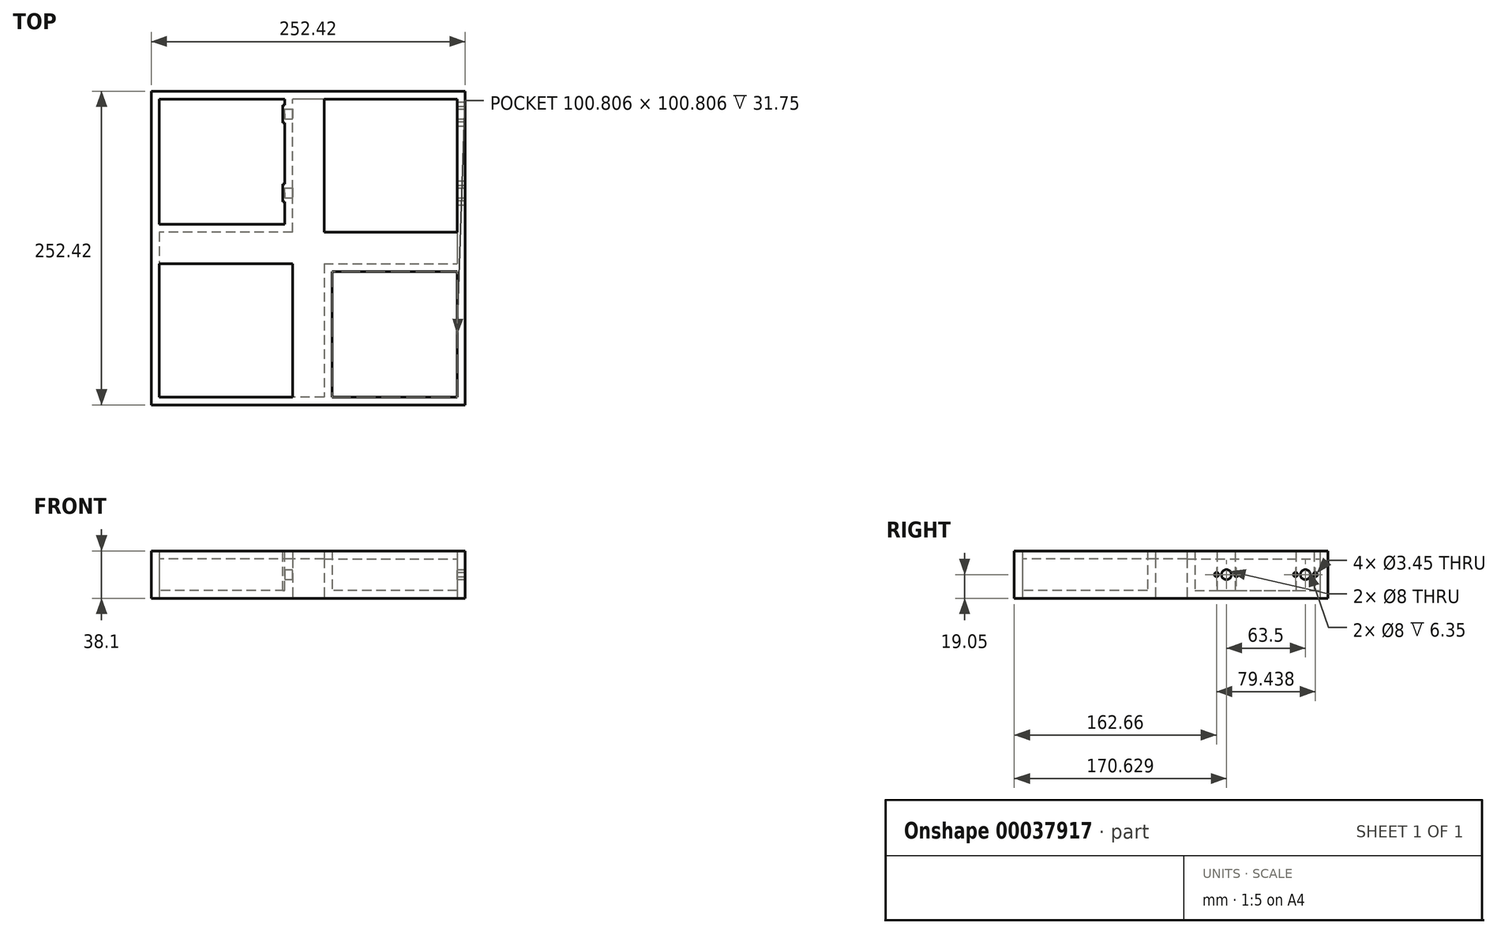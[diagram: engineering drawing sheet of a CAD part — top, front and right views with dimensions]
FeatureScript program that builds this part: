
annotation { "Feature Type Name" : "Feature", "Feature Type Description" : "" }
export const myFeature = defineFeature(function(context is Context, id is Id, definition is map)
    precondition{}
    {
        {
            var Q0;
            Q0=qCreatedBy(makeId("Top.planeOp"),FACE);
            var sketch = newSketch(context, id + "F0", { "sketchPlane" : qUnion([Q0])});
            skLineSegment(sketch, "E0.rect.bottom", {"start": v(126.2, -126.2) * mm, "end": v(-126.2, -126.2) * mm});
            skLineSegment(sketch, "E0.rect.top", {"start": v(126.2, 126.2) * mm, "end": v(-126.2, 126.2) * mm});
            skLineSegment(sketch, "E0.rect.left", {"start": v(126.2, -126.2) * mm, "end": v(126.2, 126.2) * mm});
            skLineSegment(sketch, "E0.rect.right", {"start": v(-126.2, -126.2) * mm, "end": v(-126.2, 126.2) * mm});
            skPoint(sketch, "E0.rect.middle", {"position": v(0, 0) * mm});
            skLineSegment(sketch, "E1.rect.top", {"start": v(12.7, -119.86) * mm, "end": v(-119.86, -119.86) * mm});
            skLineSegment(sketch, "E1.rect.left", {"start": v(119.86, 119.86) * mm, "end": v(119.86, -12.7) * mm});
            skLineSegment(sketch, "E1.rect.right", {"start": v(-119.86, 12.7) * mm, "end": v(-119.86, -119.86) * mm});
            skLineSegment(sketch, "E2", {"start": v(119.86, 119.86) * mm, "end": v(119.86, 126.2) * mm, "construction": true});
            skLineSegment(sketch, "E3", {"start": v(119.86, 119.86) * mm, "end": v(126.2, 119.86) * mm, "construction": true});
            skLineSegment(sketch, "E4.rect.bottom", {"start": v(-12.7, 12.7) * mm, "end": v(12.7, 12.7) * mm, "construction": true});
            skLineSegment(sketch, "E4.rect.top", {"start": v(-12.7, -12.7) * mm, "end": v(12.7, -12.7) * mm, "construction": true});
            skLineSegment(sketch, "E4.rect.left", {"start": v(-12.7, 12.7) * mm, "end": v(-12.7, -12.7) * mm, "construction": true});
            skLineSegment(sketch, "E4.rect.right", {"start": v(12.7, 12.7) * mm, "end": v(12.7, -12.7) * mm, "construction": true});
            skLineSegment(sketch, "E5.bottom", {"start": v(-12.7, 12.7) * mm, "end": v(-119.86, 12.7) * mm});
            skLineSegment(sketch, "E5.left", {"start": v(-12.7, 12.7) * mm, "end": v(-12.7, 119.86) * mm});
            skLineSegment(sketch, "E6", {"start": v(119.86, 119.86) * mm, "end": v(-12.7, 119.86) * mm});
            skLineSegment(sketch, "E7.bottom", {"start": v(-19.05, 19.05) * mm, "end": v(-119.86, 19.05) * mm});
            skLineSegment(sketch, "E7.top", {"start": v(-19.05, 119.86) * mm, "end": v(-119.86, 119.86) * mm});
            skLineSegment(sketch, "E7.left", {"start": v(-19.05, 19.05) * mm, "end": v(-19.05, 119.86) * mm});
            skLineSegment(sketch, "E7.right", {"start": v(-119.86, 19.05) * mm, "end": v(-119.86, 119.86) * mm});
            skLineSegment(sketch, "E8", {"start": v(-12.7, 119.86) * mm, "end": v(-19.05, 119.86) * mm, "construction": true});
            skLineSegment(sketch, "E9", {"start": v(-119.86, 12.7) * mm, "end": v(-119.86, 19.05) * mm, "construction": true});
            skLineSegment(sketch, "E10.bottom", {"start": v(12.7, -12.7) * mm, "end": v(119.86, -12.7) * mm});
            skLineSegment(sketch, "E10.left", {"start": v(12.7, -12.7) * mm, "end": v(12.7, -119.86) * mm});
            skLineSegment(sketch, "E11", {"start": v(119.86, -12.7) * mm, "end": v(119.86, -19.05) * mm, "construction": true});
            skLineSegment(sketch, "E12", {"start": v(12.7, -119.86) * mm, "end": v(19.05, -119.86) * mm, "construction": true});
            skLineSegment(sketch, "E13.bottom", {"start": v(119.86, -19.05) * mm, "end": v(19.05, -19.05) * mm});
            skLineSegment(sketch, "E13.top", {"start": v(119.86, -119.86) * mm, "end": v(19.05, -119.86) * mm});
            skLineSegment(sketch, "E13.left", {"start": v(119.86, -19.05) * mm, "end": v(119.86, -119.86) * mm});
            skLineSegment(sketch, "E13.right", {"start": v(19.05, -19.05) * mm, "end": v(19.05, -119.86) * mm});
            skSolve(sketch);
        }
        {
            var Q0;
            Q0 = qSketchRegion(id + "F0", true);
            extrude(context, id + "F1", {"entities" : qUnion([Q0]), "depth" : 25.4 * mm});
        }
        {
            var Q0;
            Q0=makeQuery(id+"F1.opExtrude","CAP_FACE",FACE,{"disambiguationData":[OSD([sQuery(id+"F0.wireOp",EDGE,"E0.rect.bottom"),sQuery(id+"F0.wireOp",EDGE,"E0.rect.top"),sQuery(id+"F0.wireOp",EDGE,"E0.rect.left"),sQuery(id+"F0.wireOp",EDGE,"E0.rect.right"),sQuery(id+"F0.wireOp",EDGE,"E1.rect.bottom"),sQuery(id+"F0.wireOp",EDGE,"E1.rect.top"),sQuery(id+"F0.wireOp",EDGE,"E1.rect.left"),sQuery(id+"F0.wireOp",EDGE,"E1.rect.right")])],"isStart":false});
            var sketch = newSketch(context, id + "F2", { "sketchPlane" : qUnion([Q0])});
            skLineSegment(sketch, "E14.bottom", {"start": v(-126.2, 126.2) * mm, "end": v(12.7, 126.2) * mm});
            skLineSegment(sketch, "E14.top", {"start": v(-126.2, -12.7) * mm, "end": v(-12.7, -12.7) * mm});
            skLineSegment(sketch, "E14.left", {"start": v(-126.2, 126.2) * mm, "end": v(-126.2, -12.7) * mm});
            skLineSegment(sketch, "E14.right", {"start": v(12.7, 126.2) * mm, "end": v(12.7, 12.7) * mm});
            skLineSegment(sketch, "E15.bottom", {"start": v(126.2, -126.2) * mm, "end": v(-12.7, -126.2) * mm});
            skLineSegment(sketch, "E15.top", {"start": v(126.2, 12.7) * mm, "end": v(12.7, 12.7) * mm});
            skLineSegment(sketch, "E15.left", {"start": v(126.2, -126.2) * mm, "end": v(126.2, 12.7) * mm});
            skLineSegment(sketch, "E15.right", {"start": v(-12.7, -126.2) * mm, "end": v(-12.7, -12.7) * mm});
            skLineSegment(sketch, "E16.bottom", {"start": v(-12.7, -12.7) * mm, "end": v(12.7, -12.7) * mm, "construction": true});
            skLineSegment(sketch, "E16.top", {"start": v(-12.7, 12.7) * mm, "end": v(12.7, 12.7) * mm, "construction": true});
            skLineSegment(sketch, "E16.left", {"start": v(-12.7, -12.7) * mm, "end": v(-12.7, 12.7) * mm, "construction": true});
            skLineSegment(sketch, "E16.right", {"start": v(12.7, -12.7) * mm, "end": v(12.7, 12.7) * mm, "construction": true});
            skSolve(sketch);
        }
        {
            var Q0;
            {var subQ7=sQuery(id+"F2.wireOp",EDGE,"E15.bottom");Q0=makeQuery(id+"F2.imprint","IMPRINT",FACE,{"disambiguationData":[TD([[makeQuery(id+"F2.imprint","IMPRINT",EDGE,{"derivedFrom":subQ7}),-1.0]])]});}
            var Q1;
            {var subQ8=sQuery(id+"F2.wireOp",EDGE,"E14.bottom");Q1=makeQuery(id+"F2.imprint","IMPRINT",FACE,{"disambiguationData":[TD([[makeQuery(id+"F2.imprint","IMPRINT",EDGE,{"derivedFrom":subQ8}),1.0]])]});}
            var Q2;
            {var subQ11=makeQuery(id+"F1.opExtrude","CAP_EDGE",EDGE,{"disambiguationData":[OSD([sQuery(id+"F0.wireOp",EDGE,"E5.bottom")])],"isStart":false});Q2=makeQuery(id+"F2.imprint","IMPRINT",FACE,{"disambiguationData":[TD([[makeQuery(id+"F2.imprint","IMPRINT",EDGE,{"derivedFrom":subQ11}),1.0]])]});}
            var Q3;
            {var subQ0=makeQuery(id+"F1.opExtrude","CAP_EDGE",EDGE,{"disambiguationData":[OSD([sQuery(id+"F0.wireOp",EDGE,"E1.rect.right")])],"isStart":false});var subQ3=makeQuery(id+"F1.opExtrude","CAP_EDGE",EDGE,{"disambiguationData":[OSD([sQuery(id+"F0.wireOp",EDGE,"E1.rect.top")])],"isStart":false});var subQ4=makeQuery(id+"F2.imprint","INTERSECT",VERTEX,{"derivedFrom":[subQ3,subQ0]});Q3=makeQuery(id+"F2.imprint","IMPRINT",FACE,{"disambiguationData":[TD([[makeQuery(id+"F2.imprint","IMPRINT",EDGE,{"disambiguationData":[TD([[subQ4,1.0]])],"derivedFrom":subQ3}),1.0]])]});}
            var Q4;
            {var subQ0=makeQuery(id+"F1.opExtrude","CAP_EDGE",EDGE,{"disambiguationData":[OSD([sQuery(id+"F0.wireOp",EDGE,"E6")])],"isStart":false});var subQ3=makeQuery(id+"F1.opExtrude","CAP_EDGE",EDGE,{"disambiguationData":[OSD([sQuery(id+"F0.wireOp",EDGE,"E1.rect.left")])],"isStart":false});var subQ4=makeQuery(id+"F2.imprint","INTERSECT",VERTEX,{"derivedFrom":[subQ3,subQ0]});Q4=makeQuery(id+"F2.imprint","IMPRINT",FACE,{"disambiguationData":[TD([[makeQuery(id+"F2.imprint","IMPRINT",EDGE,{"disambiguationData":[TD([[subQ4,-1.0]])],"derivedFrom":subQ3}),1.0]])]});}
            extrude(context, id + "F3", {"entities" : qUnion([Q0, Q1, Q2, Q3, Q4]), "operationType" : NewBodyOperationType.ADD, "depth" : 6.35 * mm});
        }
        {
            var Q0;
            Q0=makeQuery(id+"F3.boolean.opBoolean","MERGE",FACE,{"derivedFrom":[makeQuery(id+"F1.opExtrude","SWEPT_FACE",FACE,{"disambiguationData":[OSD([sQuery(id+"F0.wireOp",EDGE,"E0.rect.left")])]}),makeQuery(id+"F3.opExtrude","SWEPT_FACE",FACE,{"disambiguationData":[OSD([sQuery(id+"F2.wireOp",EDGE,"E15.left")])]})]});
            var sketch = newSketch(context, id + "F4", { "sketchPlane" : qUnion([Q0])});
            skLineSegment(sketch, "E17", {"start": v(126.2, 15.88) * mm, "end": v(115.89, 12.7) * mm, "construction": true});
            skLineSegment(sketch, "E18", {"start": v(115.89, 12.7) * mm, "end": v(99.95, 12.7) * mm, "construction": true});
            skLineSegment(sketch, "E19", {"start": v(99.95, 12.7) * mm, "end": v(52.39, 12.7) * mm, "construction": true});
            skLineSegment(sketch, "E20", {"start": v(52.39, 12.7) * mm, "end": v(36.45, 12.7) * mm, "construction": true});
            skCircle(sketch, "E21", {"center": v(107.92, 12.7) * mm, "radius": 4 * mm});
            skCircle(sketch, "E22", {"center": v(115.89, 12.7) * mm, "radius": 1.73 * mm});
            skCircle(sketch, "E23", {"center": v(99.95, 12.7) * mm, "radius": 1.73 * mm});
            skCircle(sketch, "E24", {"center": v(44.42, 12.7) * mm, "radius": 4 * mm});
            skCircle(sketch, "E25", {"center": v(52.39, 12.7) * mm, "radius": 1.73 * mm});
            skCircle(sketch, "E26", {"center": v(36.45, 12.7) * mm, "radius": 1.73 * mm});
            skCircle(sketch, "E27", {"center": v(115.89, 12.7) * mm, "radius": 3.97 * mm, "construction": true});
            skSolve(sketch);
        }
        {
            var Q0;
            Q0 = qSketchRegion(id + "F4", true);
            var Q1;
            Q1=makeQuery(id+"F1.opExtrude","SWEPT_FACE",FACE,{"disambiguationData":[OSD([sQuery(id+"F0.wireOp",EDGE,"E1.rect.left")])]});
            extrude(context, id + "F5", {"entities" : qUnion([Q0]), "operationType" : NewBodyOperationType.REMOVE, "endBound" : BoundingType.UP_TO_SURFACE, "oppositeDirection" : true, "endBoundEntityFace" : qUnion([Q1]), "depth" : 25.4 * mm});
        }
        {
            var Q0;
            {var subQ0=sQuery(id+"F0.wireOp",EDGE,"E7.left");Q0=makeQuery(id+"F3.boolean.opBoolean","MERGE",FACE,{"derivedFrom":[makeQuery(id+"F1.opExtrude","SWEPT_FACE",FACE,{"disambiguationData":[OSD([subQ0])]}),makeQuery(id+"F3.opExtrude","SWEPT_FACE",FACE,{"disambiguationData":[OSD([subQ0])]})]});}
            var sketch = newSketch(context, id + "F6", { "sketchPlane" : qUnion([Q0])});
            skCircle(sketch, "E28", {"center": v(-107.92, 12.7) * mm, "radius": 4 * mm, "construction": true});
            skCircle(sketch, "E29", {"center": v(-44.42, 12.7) * mm, "radius": 4 * mm, "construction": true});
            skLineSegment(sketch, "E30.bottom", {"start": v(-51.6, 0) * mm, "end": v(-37.24, 0) * mm});
            skLineSegment(sketch, "E30.top", {"start": v(-51.6, 31.75) * mm, "end": v(-37.24, 31.75) * mm});
            skLineSegment(sketch, "E30.left", {"start": v(-51.6, 0) * mm, "end": v(-51.6, 31.75) * mm});
            skLineSegment(sketch, "E30.right", {"start": v(-37.24, 0) * mm, "end": v(-37.24, 31.75) * mm});
            skLineSegment(sketch, "E31.bottom", {"start": v(-115.1, 0) * mm, "end": v(-100.74, 0) * mm});
            skLineSegment(sketch, "E31.top", {"start": v(-115.1, 31.75) * mm, "end": v(-100.74, 31.75) * mm});
            skLineSegment(sketch, "E31.left", {"start": v(-115.1, 0) * mm, "end": v(-115.1, 31.75) * mm});
            skLineSegment(sketch, "E31.right", {"start": v(-100.74, 0) * mm, "end": v(-100.74, 31.75) * mm});
            skLineSegment(sketch, "E32", {"start": v(-107.92, 31.75) * mm, "end": v(-107.92, 12.7) * mm, "construction": true});
            skLineSegment(sketch, "E33", {"start": v(-44.42, 31.75) * mm, "end": v(-44.42, 12.7) * mm, "construction": true});
            skSolve(sketch);
        }
        {
            var Q0;
            Q0 = qSketchRegion(id + "F6", true);
            var Q1;
            Q1=makeQuery(id+"F6.imprint","IMPRINT",FACE,{"disambiguationData":[TD([[makeQuery(id+"F6.imprint","IMPRINT",EDGE,{"derivedFrom":sQuery(id+"F6.wireOp",EDGE,"E29")}),1.0]])]});
            extrude(context, id + "F7", {"entities" : qUnion([Q0, Q1]), "operationType" : NewBodyOperationType.ADD, "depth" : 1.59 * mm});
        }
        {
            var Q0;
            Q0=makeQuery(id+"F1.opExtrude","SWEPT_FACE",FACE,{"disambiguationData":[OSD([sQuery(id+"F0.wireOp",EDGE,"E5.left")])]});
            var sketch = newSketch(context, id + "F8", { "sketchPlane" : qUnion([Q0])});
            skCircle(sketch, "E34", {"center": v(44.42, 12.7) * mm, "radius": 4 * mm});
            skCircle(sketch, "E35", {"center": v(107.92, 12.7) * mm, "radius": 4 * mm});
            skSolve(sketch);
        }
        {
            var Q0;
            Q0 = qSketchRegion(id + "F8", true);
            var Q1;
            {var subQ0=sQuery(id+"F0.wireOp",EDGE,"E7.left");Q1=makeQuery(id+"F7.boolean.opBoolean","SPLIT",FACE,{"disambiguationData":[TD([makeQuery(id+"F7.opExtrude","SWEPT_FACE",FACE,{"disambiguationData":[OSD([sQuery(id+"F6.wireOp",EDGE,"E30.left")])]})])],"derivedFrom":makeQuery(id+"F3.boolean.opBoolean","MERGE",FACE,{"derivedFrom":[makeQuery(id+"F1.opExtrude","SWEPT_FACE",FACE,{"disambiguationData":[OSD([subQ0])]}),makeQuery(id+"F3.opExtrude","SWEPT_FACE",FACE,{"disambiguationData":[OSD([subQ0])]})]})});}
            extrude(context, id + "F9", {"entities" : qUnion([Q0]), "operationType" : NewBodyOperationType.REMOVE, "endBound" : BoundingType.UP_TO_SURFACE, "oppositeDirection" : true, "endBoundEntityFace" : qUnion([Q1]), "depth" : 25.4 * mm});
        }
        {
            var Q0;
            Q0=makeQuery(id+"F7.boolean.opBoolean","MERGE",FACE,{"derivedFrom":[makeQuery(id+"F1.opExtrude","CAP_FACE",FACE,{"disambiguationData":[OSD([sQuery(id+"F0.wireOp",EDGE,"E0.rect.bottom"),sQuery(id+"F0.wireOp",EDGE,"E0.rect.top"),sQuery(id+"F0.wireOp",EDGE,"E0.rect.left"),sQuery(id+"F0.wireOp",EDGE,"E0.rect.right"),sQuery(id+"F0.wireOp",EDGE,"E1.rect.top"),sQuery(id+"F0.wireOp",EDGE,"E1.rect.left"),sQuery(id+"F0.wireOp",EDGE,"E1.rect.right"),sQuery(id+"F0.wireOp",EDGE,"E5.bottom"),sQuery(id+"F0.wireOp",EDGE,"E5.left"),sQuery(id+"F0.wireOp",EDGE,"E6"),sQuery(id+"F0.wireOp",EDGE,"E7.bottom"),sQuery(id+"F0.wireOp",EDGE,"E7.top"),sQuery(id+"F0.wireOp",EDGE,"E7.left"),sQuery(id+"F0.wireOp",EDGE,"E7.right"),sQuery(id+"F0.wireOp",EDGE,"E10.bottom"),sQuery(id+"F0.wireOp",EDGE,"E10.left"),sQuery(id+"F0.wireOp",EDGE,"E13.bottom"),sQuery(id+"F0.wireOp",EDGE,"E13.top"),sQuery(id+"F0.wireOp",EDGE,"E13.left"),sQuery(id+"F0.wireOp",EDGE,"E13.right")])],"isStart":true}),makeQuery(id+"F7.opExtrude","SWEPT_FACE",FACE,{"disambiguationData":[OSD([sQuery(id+"F6.wireOp",EDGE,"E30.bottom")])]}),makeQuery(id+"F7.opExtrude","SWEPT_FACE",FACE,{"disambiguationData":[OSD([sQuery(id+"F6.wireOp",EDGE,"E31.bottom")])]})]});
            var sketch = newSketch(context, id + "F10", { "sketchPlane" : qUnion([Q0])});
            skLineSegment(sketch, "E36.bottom", {"start": v(-19.05, -19.05) * mm, "end": v(-119.86, -19.05) * mm});
            skLineSegment(sketch, "E36.top", {"start": v(-19.05, -119.86) * mm, "end": v(-119.86, -119.86) * mm});
            skLineSegment(sketch, "E36.left", {"start": v(-19.05, -19.05) * mm, "end": v(-19.05, -119.86) * mm});
            skLineSegment(sketch, "E36.right", {"start": v(-119.86, -19.05) * mm, "end": v(-119.86, -119.86) * mm});
            skLineSegment(sketch, "E37.bottom", {"start": v(-126.2, 126.2) * mm, "end": v(126.2, 126.2) * mm});
            skLineSegment(sketch, "E37.top", {"start": v(-126.2, -126.2) * mm, "end": v(126.2, -126.2) * mm});
            skLineSegment(sketch, "E37.left", {"start": v(-126.2, 126.2) * mm, "end": v(-126.2, -126.2) * mm});
            skLineSegment(sketch, "E37.right", {"start": v(126.2, 126.2) * mm, "end": v(126.2, -126.2) * mm});
            skLineSegment(sketch, "E38.bottom", {"start": v(19.05, 19.05) * mm, "end": v(119.86, 19.05) * mm});
            skLineSegment(sketch, "E38.top", {"start": v(19.05, 119.86) * mm, "end": v(119.86, 119.86) * mm});
            skLineSegment(sketch, "E38.left", {"start": v(19.05, 19.05) * mm, "end": v(19.05, 119.86) * mm});
            skLineSegment(sketch, "E38.right", {"start": v(119.86, 19.05) * mm, "end": v(119.86, 119.86) * mm});
            skLineSegment(sketch, "E39.bottom", {"start": v(12.7, 119.86) * mm, "end": v(-119.86, 119.86) * mm});
            skLineSegment(sketch, "E39.top", {"start": v(-12.7, -12.7) * mm, "end": v(-119.86, -12.7) * mm});
            skLineSegment(sketch, "E39.left", {"start": v(12.7, 119.86) * mm, "end": v(12.7, 12.7) * mm});
            skLineSegment(sketch, "E39.right", {"start": v(-119.86, 119.86) * mm, "end": v(-119.86, -12.7) * mm});
            skLineSegment(sketch, "E40.bottom", {"start": v(-12.7, -119.86) * mm, "end": v(119.86, -119.86) * mm});
            skLineSegment(sketch, "E40.top", {"start": v(12.7, 12.7) * mm, "end": v(119.86, 12.7) * mm});
            skLineSegment(sketch, "E40.left", {"start": v(-12.7, -119.86) * mm, "end": v(-12.7, -12.7) * mm});
            skLineSegment(sketch, "E40.right", {"start": v(119.86, -119.86) * mm, "end": v(119.86, 12.7) * mm});
            skSolve(sketch);
        }
        {
            var Q0;
            {var subQ6=sQuery(id+"F10.wireOp",EDGE,"E36.bottom");Q0=makeQuery(id+"F10.imprint","IMPRINT",FACE,{"disambiguationData":[TD([[makeQuery(id+"F10.imprint","IMPRINT",EDGE,{"derivedFrom":subQ6}),1.0]])]});}
            var Q1;
            Q1=makeQuery(id+"F10.imprint","IMPRINT",FACE,{"disambiguationData":[TD([[makeQuery(id+"F10.imprint","IMPRINT",EDGE,{"derivedFrom":sQuery(id+"F10.wireOp",EDGE,"E38.bottom")}),-1.0]])]});
            var Q2;
            {var subQ9=sQuery(id+"F10.wireOp",EDGE,"E36.bottom");Q2=makeQuery(id+"F10.imprint","IMPRINT",FACE,{"disambiguationData":[TD([[makeQuery(id+"F10.imprint","IMPRINT",EDGE,{"derivedFrom":subQ9}),-1.0]])]});}
            var Q3;
            {var subQ1=sQuery(id+"F6.wireOp",EDGE,"E30.bottom");Q3=makeQuery(id+"F10.imprint","IMPRINT",FACE,{"disambiguationData":[TD([[makeQuery(id+"F10.imprint","IMPRINT",EDGE,{"derivedFrom":makeQuery(id+"F7.opExtrude","CAP_EDGE",EDGE,{"disambiguationData":[OSD([subQ1])],"isStart":false})}),1.0]])]});}
            var Q4;
            {var subQ0=sQuery(id+"F6.wireOp",EDGE,"E31.bottom");Q4=makeQuery(id+"F10.imprint","IMPRINT",FACE,{"disambiguationData":[TD([[makeQuery(id+"F10.imprint","IMPRINT",EDGE,{"derivedFrom":makeQuery(id+"F7.opExtrude","CAP_EDGE",EDGE,{"disambiguationData":[OSD([subQ0])],"isStart":false})}),1.0]])]});}
            extrude(context, id + "F11", {"entities" : qUnion([Q0, Q1, Q2, Q3, Q4]), "operationType" : NewBodyOperationType.ADD, "depth" : 6.35 * mm});
        }
    });
